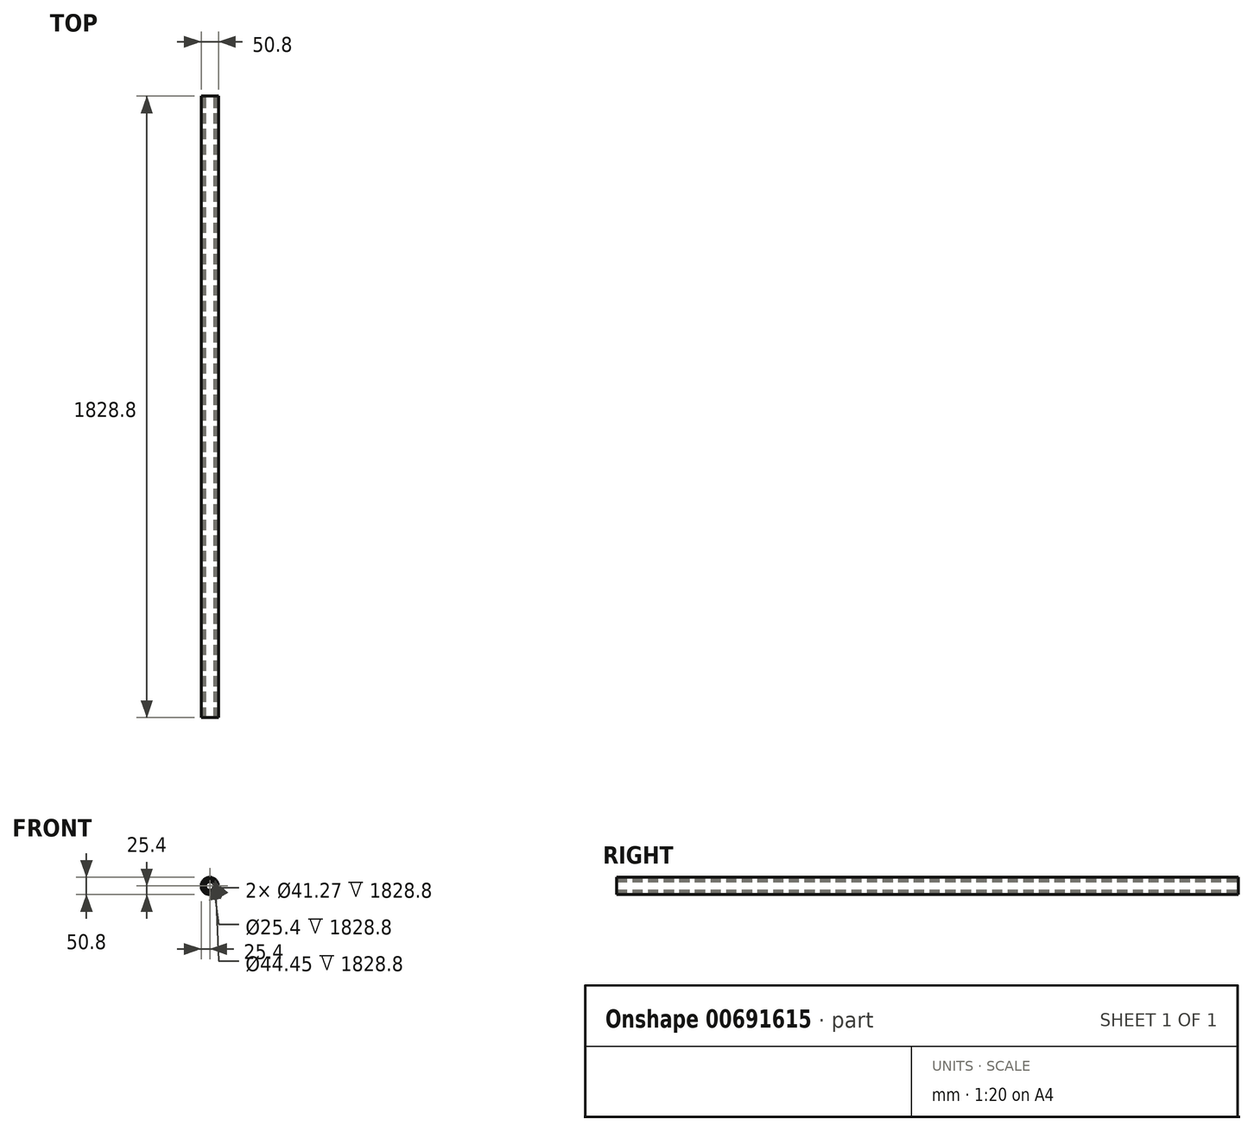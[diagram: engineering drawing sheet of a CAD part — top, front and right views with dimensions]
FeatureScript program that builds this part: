
annotation { "Feature Type Name" : "Feature", "Feature Type Description" : "" }
export const myFeature = defineFeature(function(context is Context, id is Id, definition is map)
    precondition{}
    {
        {
            var Q0;
            Q0=qCreatedBy(makeId("Front.planeOp"),FACE);
            var sketch = newSketch(context, id + "F0", { "sketchPlane" : qUnion([Q0])});
            skCircle(sketch, "E0", {"center": v(0, 0) * mm, "radius": 22.23 * mm});
            skCircle(sketch, "E1", {"center": v(0, 0) * mm, "radius": 25.4 * mm});
            skSolve(sketch);
        }
        {
            var Q0;
            Q0=qCreatedBy(makeId("Front.planeOp"),FACE);
            var sketch = newSketch(context, id + "F1", { "sketchPlane" : qUnion([Q0])});
            skCircle(sketch, "E2", {"center": v(0, 0) * mm, "radius": 22.23 * mm});
            skCircle(sketch, "E3", {"center": v(0, 0) * mm, "radius": 20.64 * mm});
            skSolve(sketch);
        }
        {
            var Q0;
            Q0=qCreatedBy(makeId("Front.planeOp"),FACE);
            var sketch = newSketch(context, id + "F2", { "sketchPlane" : qUnion([Q0])});
            skArc(sketch, "E4", {"start": v(7.09, 19.3) * mm, "mid": v(12.53, 16.08) * mm, "end": v(16.9, 11.5) * mm});
            skArc(sketch, "E5", {"start": v(5.3, 15.8) * mm, "mid": v(10.22, 12.92) * mm, "end": v(14.06, 8.7) * mm});
            skLineSegment(sketch, "E6", {"start": v(7.09, 19.3) * mm, "end": v(5.3, 15.8) * mm});
            skLineSegment(sketch, "E7", {"start": v(16.9, 11.5) * mm, "end": v(14.06, 8.7) * mm});
            skArc(sketch, "E8.MirrorCS", {"start": v(7.09, -19.3) * mm, "mid": v(12.53, -16.08) * mm, "end": v(16.9, -11.5) * mm});
            skLineSegment(sketch, "E9.MirrorCS", {"start": v(7.09, -19.3) * mm, "end": v(5.3, -15.8) * mm});
            skLineSegment(sketch, "E10.MirrorCS", {"start": v(16.9, -11.5) * mm, "end": v(14.06, -8.7) * mm});
            skArc(sketch, "E11.MirrorCS", {"start": v(5.3, -15.8) * mm, "mid": v(10.22, -12.92) * mm, "end": v(14.06, -8.7) * mm});
            skArc(sketch, "E12.MirrorCS", {"start": v(-7.09, 19.3) * mm, "mid": v(-12.53, 16.08) * mm, "end": v(-16.9, 11.5) * mm});
            skLineSegment(sketch, "E13.MirrorCS", {"start": v(-7.09, 19.3) * mm, "end": v(-5.3, 15.8) * mm});
            skLineSegment(sketch, "E14.MirrorCS", {"start": v(-16.9, 11.5) * mm, "end": v(-14.06, 8.7) * mm});
            skArc(sketch, "E15.MirrorCS", {"start": v(-5.3, 15.8) * mm, "mid": v(-10.22, 12.92) * mm, "end": v(-14.06, 8.7) * mm});
            skArc(sketch, "E16.MirrorCS", {"start": v(-7.09, -19.3) * mm, "mid": v(-12.53, -16.08) * mm, "end": v(-16.9, -11.5) * mm});
            skArc(sketch, "E17.MirrorCS", {"start": v(-5.3, -15.8) * mm, "mid": v(-10.22, -12.92) * mm, "end": v(-14.06, -8.7) * mm});
            skLineSegment(sketch, "E18.MirrorCS", {"start": v(-16.9, -11.5) * mm, "end": v(-14.06, -8.7) * mm});
            skLineSegment(sketch, "E19.MirrorCS", {"start": v(-7.09, -19.3) * mm, "end": v(-5.3, -15.8) * mm});
            skPoint(sketch, "E20", {"position": v(0, 0) * mm});
            skCircle(sketch, "E21.0", {"center": v(0, 0) * mm, "radius": 22.23 * mm});
            skCircle(sketch, "E22.0", {"center": v(0, 0) * mm, "radius": 20.64 * mm});
            skSolve(sketch);
        }
        {
            var Q0;
            Q0=qCreatedBy(makeId("Front.planeOp"),FACE);
            var sketch = newSketch(context, id + "F3", { "sketchPlane" : qUnion([Q0])});
            skCircle(sketch, "E23", {"center": v(0, 0) * mm, "radius": 16.7 * mm});
            skCircle(sketch, "E24", {"center": v(0, 0) * mm, "radius": 12.7 * mm});
            skSolve(sketch);
        }
        {
            var Q0;
            Q0 = qSketchRegion(id + "F2", true);
            extrude(context, id + "F4", {"entities" : qUnion([Q0]), "endBound" : BoundingType.SYMMETRIC, "depth" : 1828.8 * mm, "offsetDistance" : 25.4 * mm});
        }
        {
            var Q0;
            Q0 = qSketchRegion(id + "F1", true);
            extrude(context, id + "F5", {"entities" : qUnion([Q0]), "endBound" : BoundingType.SYMMETRIC, "depth" : 1828.8 * mm, "offsetDistance" : 25.4 * mm});
        }
        {
            var Q0;
            Q0=makeQuery(id+"F0.imprint","IMPRINT",FACE,{"disambiguationData":[TD([[makeQuery(id+"F0.imprint","IMPRINT",EDGE,{"derivedFrom":sQuery(id+"F0.wireOp",EDGE,"E0")}),-1.0]])]});
            extrude(context, id + "F6", {"entities" : qUnion([Q0]), "endBound" : BoundingType.SYMMETRIC, "depth" : 1828.8 * mm, "offsetDistance" : 25.4 * mm, "hasSecondDirection" : true, "secondDirectionOppositeDirection" : true, "secondDirectionDepth" : 25.4 * mm});
        }
        {
            var Q0;
            Q0 = qSketchRegion(id + "F3", true);
            extrude(context, id + "F7", {"entities" : qUnion([Q0]), "endBound" : BoundingType.SYMMETRIC, "depth" : 1828.8 * mm, "offsetDistance" : 25.4 * mm});
        }
    });
